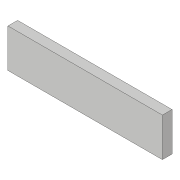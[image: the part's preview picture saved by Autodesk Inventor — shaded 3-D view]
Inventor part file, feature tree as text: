
AUTODESK INVENTOR PART (.ipt)
format: ipt  version: 2018.3 (Build 223284000, 284)  size: 72,192 bytes
history: native  units: in
note: dims shown in document units (in); Inventor stores cm internally (conversion verified against a paired STEP export)
features: extrude x1, sketch x1
ambient origin geometry x8: Origin, YZ Plane, XZ Plane, XY Plane, X Axis, Y Axis, Z Axis, Center Point
bodies: Solid1 (feature_tree)
feature tree (2):
  extrude  "Extrusion1"  Depth=0.25in
  sketch  "Sketch1"  dims[d0=1.0in d1=0.25in d2=0.0625in d3=0.0in]
